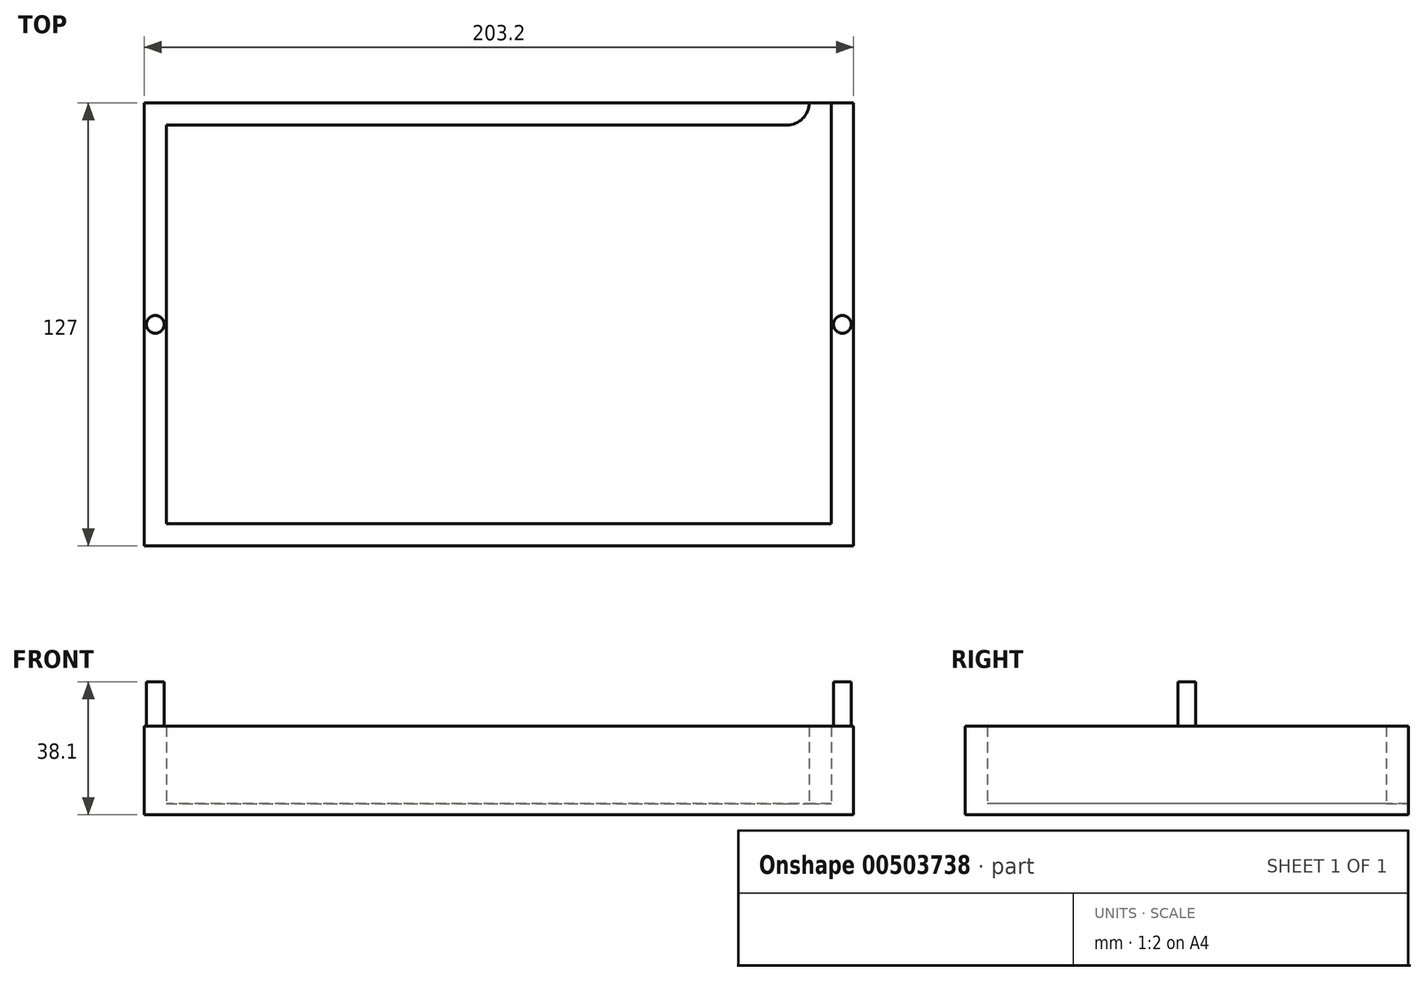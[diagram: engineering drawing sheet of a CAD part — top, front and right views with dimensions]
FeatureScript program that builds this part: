
annotation { "Feature Type Name" : "Feature", "Feature Type Description" : "" }
export const myFeature = defineFeature(function(context is Context, id is Id, definition is map)
    precondition{}
    {
        {
            var Q0;
            Q0=qCreatedBy(makeId("Top.planeOp"),FACE);
            var sketch = newSketch(context, id + "F0", { "sketchPlane" : qUnion([Q0])});
            skLineSegment(sketch, "E0.bottom", {"start": v(-101.6, 63.5) * mm, "end": v(101.6, 63.5) * mm});
            skLineSegment(sketch, "E0.top", {"start": v(-101.6, -63.5) * mm, "end": v(101.6, -63.5) * mm});
            skLineSegment(sketch, "E0.left", {"start": v(-101.6, 63.5) * mm, "end": v(-101.6, -63.5) * mm});
            skLineSegment(sketch, "E0.right", {"start": v(101.6, 63.5) * mm, "end": v(101.6, -63.5) * mm});
            skPoint(sketch, "E0.middle", {"position": v(0, 0) * mm});
            skPoint(sketch, "E1", {"position": v(101.6, 0) * mm});
            skPoint(sketch, "E2", {"position": v(-101.6, 0) * mm});
            skLineSegment(sketch, "E3", {"start": v(-101.6, 0) * mm, "end": v(101.6, 0) * mm, "construction": true});
            skLineSegment(sketch, "E4", {"start": v(95.25, 57.15) * mm, "end": v(95.25, -57.15) * mm});
            skPoint(sketch, "E5", {"position": v(95.25, 0) * mm});
            skLineSegment(sketch, "E6", {"start": v(95.25, -57.15) * mm, "end": v(-95.25, -57.15) * mm});
            skLineSegment(sketch, "E7", {"start": v(95.25, 57.15) * mm, "end": v(95.25, 63.5) * mm});
            skLineSegment(sketch, "E8", {"start": v(95.25, 63.5) * mm, "end": v(88.9, 63.5) * mm});
            skLineSegment(sketch, "E9", {"start": v(-95.25, -57.15) * mm, "end": v(-95.25, 63.5) * mm, "construction": true});
            skLineSegment(sketch, "E10", {"start": v(-95.25, 57.15) * mm, "end": v(-95.25, -57.15) * mm});
            skLineSegment(sketch, "E11", {"start": v(88.9, 63.5) * mm, "end": v(88.9, 63.5) * mm});
            skLineSegment(sketch, "E12", {"start": v(-95.25, 57.15) * mm, "end": v(82.55, 57.15) * mm});
            skPoint(sketch, "E13.visualSharp", {"position": v(88.9, 57.15) * mm});
            skArc(sketch, "E13.filletArc", {"start": v(82.55, 57.15) * mm, "mid": v(87.04, 59) * mm, "end": v(88.9, 63.5) * mm});
            skLineSegment(sketch, "E14", {"start": v(-95.25, -28.88) * mm, "end": v(-101.6, -28.88) * mm, "construction": true});
            skLineSegment(sketch, "E15", {"start": v(-42.8, -57.15) * mm, "end": v(-42.8, -63.5) * mm, "construction": true});
            skSolve(sketch);
        }
        {
            var Q0;
            Q0=makeQuery(id+"F0.imprint","IMPRINT",FACE,{"disambiguationData":[TD([[makeQuery(id+"F0.imprint","IMPRINT",EDGE,{"derivedFrom":sQuery(id+"F0.wireOp",EDGE,"E0.top")}),1.0]])]});
            extrude(context, id + "F1", {"entities" : qUnion([Q0]), "depth" : 25.4 * mm});
        }
        {
            var Q0;
            Q0=makeQuery(id+"F0.imprint","IMPRINT",FACE,{"disambiguationData":[TD([[makeQuery(id+"F0.imprint","IMPRINT",EDGE,{"derivedFrom":sQuery(id+"F0.wireOp",EDGE,"E4")}),-1.0]])]});
            extrude(context, id + "F2", {"entities" : qUnion([Q0]), "operationType" : NewBodyOperationType.ADD, "depth" : 3.17 * mm});
        }
        {
            var Q0;
            Q0=makeQuery(id+"F1.opExtrude","CAP_FACE",FACE,{"disambiguationData":[OSD([sQuery(id+"F0.wireOp",EDGE,"E0.bottom"),sQuery(id+"F0.wireOp",EDGE,"E0.top"),sQuery(id+"F0.wireOp",EDGE,"E0.left"),sQuery(id+"F0.wireOp",EDGE,"E0.right"),sQuery(id+"F0.wireOp",EDGE,"E4"),sQuery(id+"F0.wireOp",EDGE,"E6"),sQuery(id+"F0.wireOp",EDGE,"E7"),sQuery(id+"F0.wireOp",EDGE,"E10"),sQuery(id+"F0.wireOp",EDGE,"E12"),sQuery(id+"F0.wireOp",EDGE,"E13.filletArc")])],"isStart":false});
            var sketch = newSketch(context, id + "F3", { "sketchPlane" : qUnion([Q0])});
            skLineSegment(sketch, "E16", {"start": v(-95.25, 0) * mm, "end": v(-101.6, 0) * mm, "construction": true});
            skLineSegment(sketch, "E17", {"start": v(95.25, 0) * mm, "end": v(101.6, 0) * mm, "construction": true});
            skPoint(sketch, "E17.startSnap0", {"position": v(101.6, 0) * mm});
            skPoint(sketch, "E18", {"position": v(-98.43, 0) * mm});
            skCircle(sketch, "E19", {"center": v(-98.43, 0) * mm, "radius": 2.54 * mm});
            skPoint(sketch, "E20", {"position": v(98.42, 0) * mm});
            skCircle(sketch, "E21", {"center": v(98.42, 0) * mm, "radius": 2.54 * mm});
            skSolve(sketch);
        }
        {
            var Q0;
            Q0 = qSketchRegion(id + "F3", true);
            extrude(context, id + "F4", {"entities" : qUnion([Q0]), "operationType" : NewBodyOperationType.ADD, "depth" : 12.7 * mm, "offsetDistance" : 25.4 * mm});
        }
    });
